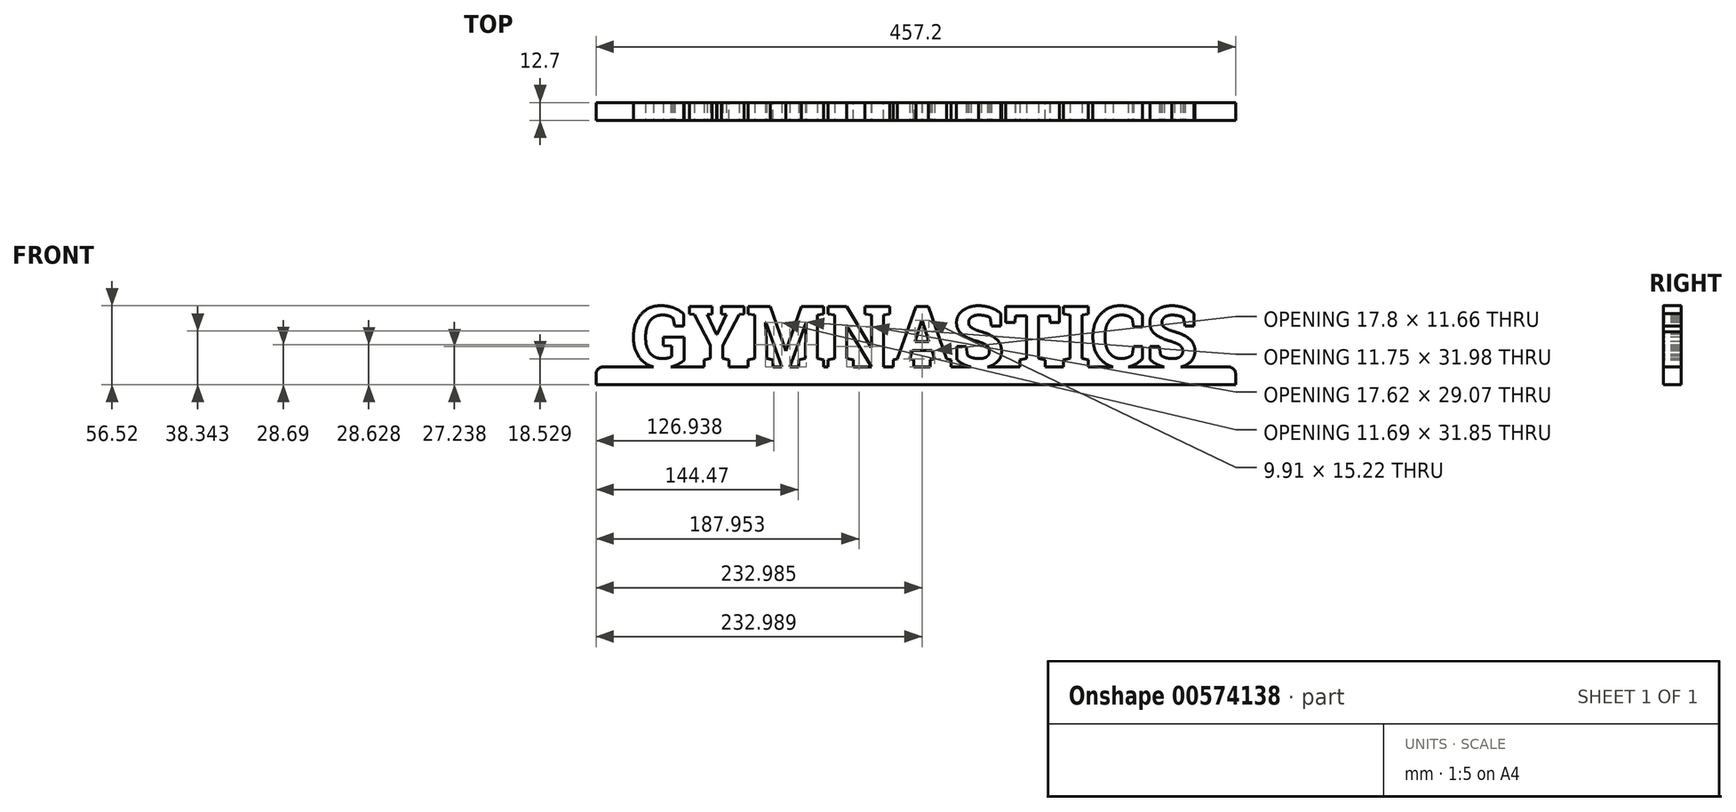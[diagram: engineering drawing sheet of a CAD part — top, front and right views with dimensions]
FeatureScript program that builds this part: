
annotation { "Feature Type Name" : "Feature", "Feature Type Description" : "" }
export const myFeature = defineFeature(function(context is Context, id is Id, definition is map)
    precondition{}
    {
        {
            var Q0;
            Q0=qCreatedBy(makeId("Front.planeOp"),FACE);
            var sketch = newSketch(context, id + "F0", { "sketchPlane" : qUnion([Q0])});
            skLineSegment(sketch, "E0.bottom", {"start": v(-211.92, -89.49) * mm, "end": v(245.28, -89.49) * mm});
            skLineSegment(sketch, "E0.top", {"start": v(-211.92, -102.19) * mm, "end": v(245.28, -102.19) * mm});
            skLineSegment(sketch, "E0.left", {"start": v(-211.92, -89.49) * mm, "end": v(-211.92, -102.19) * mm});
            skLineSegment(sketch, "E0.right", {"start": v(245.28, -89.49) * mm, "end": v(245.28, -102.19) * mm});
            skSolve(sketch);
        }
        {
            var Q0;
            Q0=makeQuery(id+"F0.imprint","IMPRINT",FACE,{"disambiguationData":[TD([[makeQuery(id+"F0.imprint","IMPRINT",EDGE,{"derivedFrom":sQuery(id+"F0.wireOp",EDGE,"E0.bottom")}),-1.0]])]});
            extrude(context, id + "F1", {"entities" : qUnion([Q0]), "depth" : 12.7 * mm, "offsetDistance" : 25.4 * mm});
        }
        {
            var Q0;
            Q0=makeQuery(id+"F1.opExtrude","CAP_FACE",FACE,{"disambiguationData":[OSD([sQuery(id+"F0.wireOp",EDGE,"E0.bottom"),sQuery(id+"F0.wireOp",EDGE,"E0.top"),sQuery(id+"F0.wireOp",EDGE,"E0.left"),sQuery(id+"F0.wireOp",EDGE,"E0.right")])],"isStart":false});
            var sketch = newSketch(context, id + "F2", { "sketchPlane" : qUnion([Q0])});
            skText(sketch, "E1", { "text": "GYMNASTICS", "fontName": "RobotoSlab-Bold.ttf"});
            skPoint(sketch, "E2", {"position": v(-186.52, -89.49) * mm});
            const initialGuessF2  = {"E1": [-0.18652, -0.08949, 1, 0, 0.04374]};
            skSetInitialGuess(sketch, initialGuessF2);
            skSolve(sketch);
        }
        {
            var Q0;
            Q0=qSketchRegion(id+"F2",true);
            extrude(context, id + "F3", {"entities" : qUnion([Q0]), "operationType" : NewBodyOperationType.ADD, "depth" : -12.7 * mm, "offsetDistance" : 25.4 * mm});
        }
        {
            var Q0;
            Q0=makeQuery(id+"F1.opExtrude","SWEPT_EDGE",EDGE,{"disambiguationData":[OSD([sQuery(id+"F0.wireOp",EDGE,"E0.bottom"),sQuery(id+"F0.wireOp",EDGE,"E0.left")])]});
            var Q1;
            Q1=makeQuery(id+"F1.opExtrude","SWEPT_EDGE",EDGE,{"disambiguationData":[OSD([sQuery(id+"F0.wireOp",EDGE,"E0.bottom"),sQuery(id+"F0.wireOp",EDGE,"E0.right")])]});
            fillet(context, id + "F4", {"entities" : qUnion([Q0, Q1]), "radius" : 5.08 * mm, "tangentPropagation" : true, "allowEdgeOverflow" : false});
        }
    });
